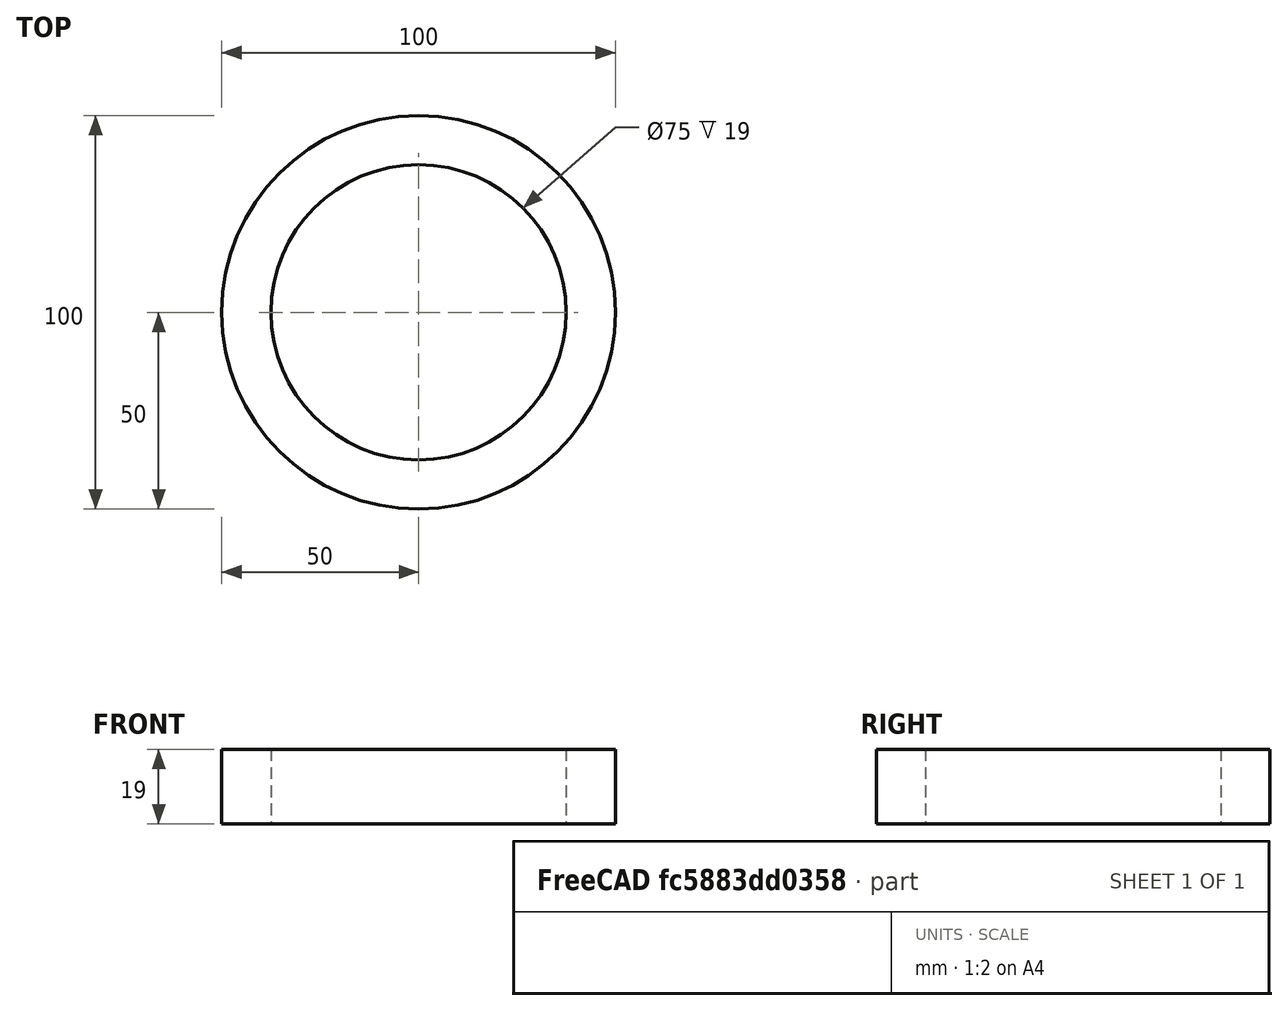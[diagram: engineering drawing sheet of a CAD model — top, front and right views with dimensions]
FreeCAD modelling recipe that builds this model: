
FCSTD DOCUMENT  (FreeCAD 1.1R38827 (Git))
Label: bearing_d100
License: All rights reserved
LicenseURL: http://en.wikipedia.org/wiki/All_rights_reserved
objects: PartDesign::CoordinateSystem×2, Sketcher::SketchObject×1, PartDesign::SubShapeBinder×1, PartDesign::Revolution×1, PartDesign::Body×1
note: 9 computed .brp shape members not serialized (recipe doc carries the construction recipe); baked Part::Feature solids carry a one-line shape summary decoded from their .brp

FEATURE [Sketcher::SketchObject] Sketch  label="main_Sketch"
  ArcFitTolerance = 0
  FullyConstrained = true
  MakeInternals = false
  Placement = pos=(0,0,0) rot=(1,0,0;1.5708rad)
  sketch-geometry (4):
    g0: LineSegment StartX=37.5 StartY=0 StartZ=0 EndX=50 EndY=0 EndZ=0
    g1: LineSegment StartX=50 StartY=0 StartZ=0 EndX=50 EndY=19 EndZ=0
    g2: LineSegment StartX=50 StartY=19 StartZ=0 EndX=37.5 EndY=19 EndZ=0
    g3: LineSegment StartX=37.5 StartY=19 StartZ=0 EndX=37.5 EndY=0 EndZ=0
  constraints (12):
    c: Coincident(g0,g1)
    c: Coincident(g1,g2)
    c: Coincident(g2,g3)
    c: Coincident(g3,g0)
    c: Horizontal(g0)
    c: Horizontal(g2)
    c: Vertical(g1)
    c: Vertical(g3)
    c: PointOnObject(g0,g-1)
    c: DistanceX(g0) = 37.5  'min_r'
    c: DistanceX(g0) = 50  'max_r'
    c: DistanceY(g3,g3) = 19  'height'
FEATURE [PartDesign::SubShapeBinder] Binder
  BindCopyOnChange = 0
  BindMode = 0
  ClaimChildren = true
  Context = -> Body [Binder.]
  Fuse = false
  MakeFace = true
  OffsetFill = false
  OffsetIntersection = false
  OffsetJoinType = 0
  OffsetOpenResult = false
  PartialLoad = false
  Placement = pos=(0,0,0) rot=(1,0,0;1.5708rad)
  Relative = false
  Support = -> [Sketch]
  _Version = 2
  expr: Placement = Support[0][0].Placement
FEATURE [PartDesign::Revolution] Revolution
  Angle = 360
  Angle2 = 60
  Axis = (1e-16,1e-16,1)
  Base = (0,0,0)
  Placement = pos=(0,0,0) rot=(1,0,0;1.5708rad)
  Profile = -> Binder [Face1]
  ReferenceAxis = -> Z_Axis
  Reversed = true
  Suppressed = false
  Type = 0
FEATURE [PartDesign::CoordinateSystem] Local_CS  label="bottom_LCS"
  AttacherType = Attacher::AttachEngine3D
  AttachmentSupport = -> [XY_Plane]
  MapMode = 5
FEATURE [PartDesign::CoordinateSystem] Local_CS001  label="top_LCS"
  AttacherType = Attacher::AttachEngine3D
  AttachmentOffset = pos=(0,0,19) rot=(0,0,1;0rad)
  AttachmentSupport = -> [XY_Plane]
  MapMode = 5
  Placement = pos=(0,0,19) rot=(0,0,1;0rad)
  expr: .AttachmentOffset.Base.z = <<main_Sketch>>.Constraints.height
FEATURE [PartDesign::Body] Body  label="bearing_d100"
  AllowCompound = false
  Group = -> [Binder,Revolution,Local_CS,Local_CS001]
  Origin = -> Origin
  Tip = -> Revolution
